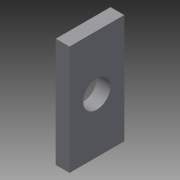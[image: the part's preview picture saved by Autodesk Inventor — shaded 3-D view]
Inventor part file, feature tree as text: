
AUTODESK INVENTOR PART (.ipt)
format: ipt  version: 2013 (Build 170138000, 138)  size: 76,800 bytes
history: native  units: in
note: dims shown in document units (in); Inventor stores cm internally (conversion verified against a paired STEP export)
features: extrude x1, sketch x1
ambient origin geometry x8: Origin, YZ Plane, XZ Plane, XY Plane, X Axis, Y Axis, Z Axis, Center Point
feature tree (2):
  extrude  "Extrusion2"  Depth=1.0in
  sketch  "Sketch1"  dims[d0=4.5in d1=1.0in d4=1.0in d5=2.5in d6=0.5in d7=0.5in d8=0.25in d9=0.0in]
